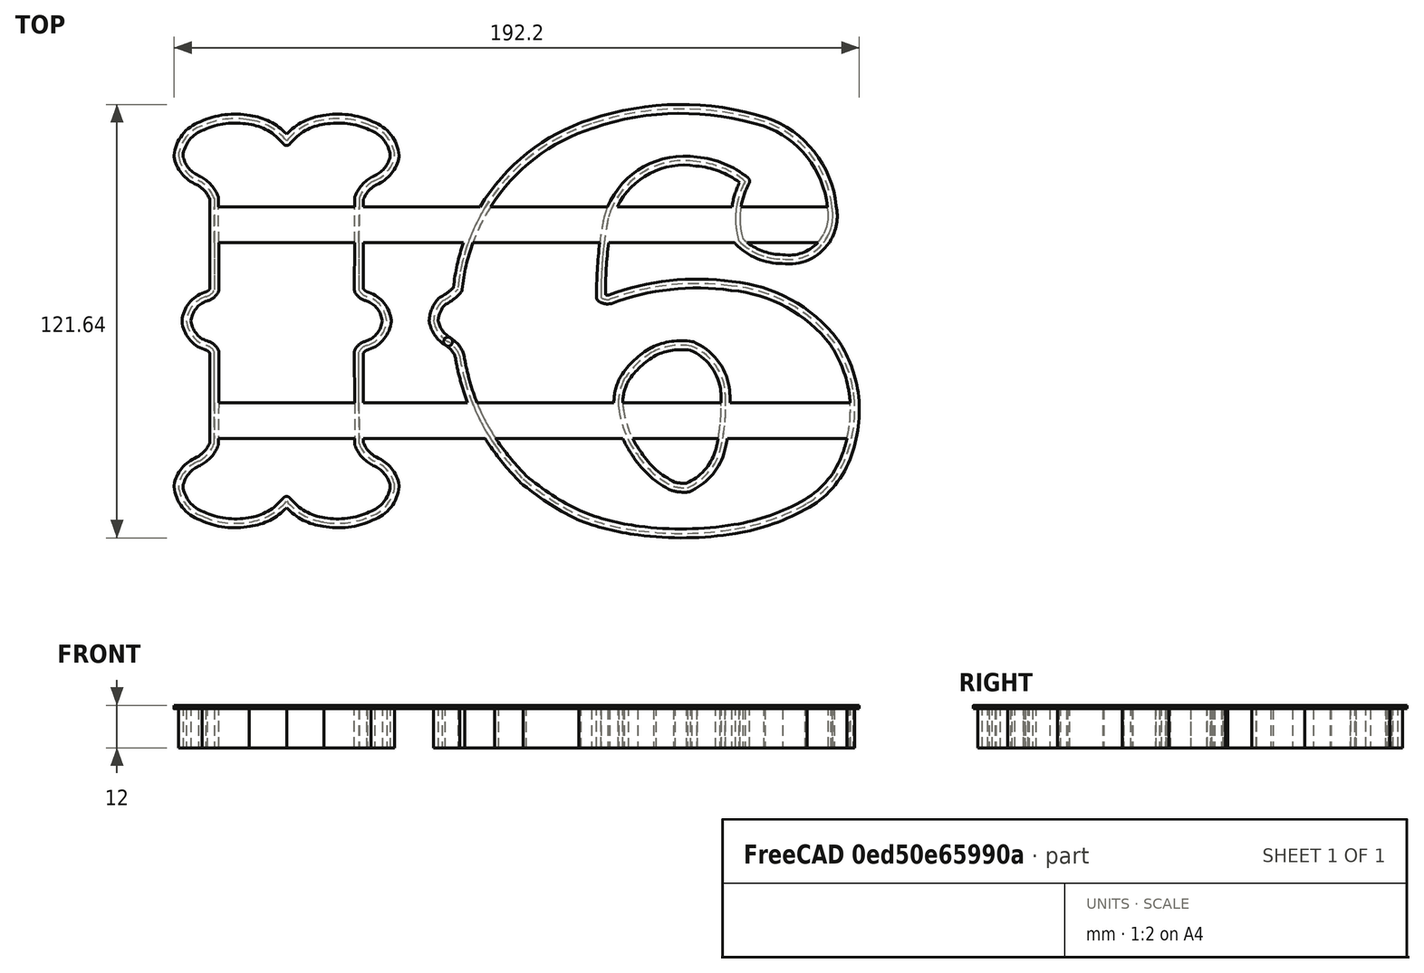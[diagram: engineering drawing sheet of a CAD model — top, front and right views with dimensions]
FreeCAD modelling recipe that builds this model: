
FCSTD DOCUMENT  (FreeCAD 0.20R27319 (Git))
Label: NumberCutter_16
License: All rights reserved
LicenseURL: http://en.wikipedia.org/wiki/All_rights_reserved
objects: Part::Offset2D×2, Part::Extrusion×2, Part::Box×2, Part::MultiFuse×2, Image::ImagePlane×1, Sketcher::SketchObject×1, PartDesign::Body×1
note: 10 computed .brp shape members not serialized (recipe doc carries the construction recipe); baked Part::Feature solids carry a one-line shape summary decoded from their .brp

FEATURE [Image::ImagePlane] ImagePlane
  XSize = 191
  YSize = 120
FEATURE [Sketcher::SketchObject] Sketch001  label="Sketch"
  FullyConstrained = false
  MapMode = 5
  Support = -> [XY_Plane]
  sketch-geometry (67):
    g0: LineSegment StartX=-44.0949 StartY=34.442 StartZ=0 EndX=-44.1561 EndY=8.72012 EndZ=0
    g1: ArcOfCircle CenterX=-44.2555 CenterY=-0.704352 CenterZ=0 NormalX=0 NormalY=0 NormalZ=1 AngleXU=0 Radius=7.94489 StartAngle=0.0887712 EndAngle=1.24847
    g2: ArcOfCircle CenterX=-41.0719 CenterY=10.1762 CenterZ=0 NormalX=0 NormalY=0 NormalZ=1 AngleXU=0 Radius=3.4106 StartAngle=3.58267 EndAngle=4.51561
    g3: ArcOfCircle CenterX=-51.9319 CenterY=40.6835 CenterZ=0 NormalX=0 NormalY=0 NormalZ=1 AngleXU=0 Radius=15.899 StartAngle=1.69919 EndAngle=2.47486
    g4: ArcOfCircle CenterX=-50.005 CenterY=34.6117 CenterZ=0 NormalX=0 NormalY=0 NormalZ=1 AngleXU=0 Radius=22.1964 StartAngle=1.13736 EndAngle=1.75028
    g5: ArcOfCircle CenterX=-43.9763 CenterY=45.3788 CenterZ=0 NormalX=0 NormalY=0 NormalZ=1 AngleXU=0 Radius=9.93843 StartAngle=0.0999134 EndAngle=1.23302
    g6: ArcOfCircle CenterX=-43.0231 CenterY=47.8373 CenterZ=0 NormalX=0 NormalY=0 NormalZ=1 AngleXU=0 Radius=9.05532 StartAngle=5.08333 EndAngle=6.12044
    g7: ArcOfCircle CenterX=-35.5185 CenterY=31.2976 CenterZ=0 NormalX=0 NormalY=0 NormalZ=1 AngleXU=0 Radius=9.13456 StartAngle=2.05128 EndAngle=2.79018
    g8: LineSegment StartX=-84.7572 StartY=34.442 StartZ=0 EndX=-84.6959 EndY=8.72012 EndZ=0
    g9: ArcOfCircle CenterX=-84.5965 CenterY=-0.704352 CenterZ=0 NormalX=0 NormalY=0 NormalZ=1 AngleXU=0 Radius=7.94489 StartAngle=1.89313 EndAngle=3.05282
    g10: ArcOfCircle CenterX=-87.7801 CenterY=10.1762 CenterZ=0 NormalX=0 NormalY=0 NormalZ=1 AngleXU=0 Radius=3.4106 StartAngle=4.90916 EndAngle=5.8421
    g11: ArcOfCircle CenterX=-76.9201 CenterY=40.6835 CenterZ=0 NormalX=0 NormalY=0 NormalZ=1 AngleXU=0 Radius=15.899 StartAngle=0.666734 EndAngle=1.4424
    g12: ArcOfCircle CenterX=-78.847 CenterY=34.6117 CenterZ=0 NormalX=0 NormalY=0 NormalZ=1 AngleXU=0 Radius=22.1964 StartAngle=1.39131 EndAngle=2.00423
    g13: ArcOfCircle CenterX=-84.8757 CenterY=45.3788 CenterZ=0 NormalX=0 NormalY=0 NormalZ=1 AngleXU=0 Radius=9.93843 StartAngle=1.90858 EndAngle=3.04168
    g14: ArcOfCircle CenterX=-85.8289 CenterY=47.8373 CenterZ=0 NormalX=0 NormalY=0 NormalZ=1 AngleXU=0 Radius=9.05532 StartAngle=3.30434 EndAngle=4.34144
    g15: ArcOfCircle CenterX=-93.3335 CenterY=31.2976 CenterZ=0 NormalX=0 NormalY=0 NormalZ=1 AngleXU=0 Radius=9.13456 StartAngle=0.35141 EndAngle=1.09032
    g16: LineSegment StartX=-44.0949 StartY=-34.442 StartZ=0 EndX=-44.1561 EndY=-8.72012 EndZ=0
    g17: ArcOfCircle CenterX=-44.2555 CenterY=0.704352 CenterZ=0 NormalX=0 NormalY=0 NormalZ=1 AngleXU=0 Radius=7.94489 StartAngle=5.03472 EndAngle=6.19441
    g18: ArcOfCircle CenterX=-41.0719 CenterY=-10.1762 CenterZ=0 NormalX=0 NormalY=0 NormalZ=1 AngleXU=0 Radius=3.4106 StartAngle=1.76757 EndAngle=2.70051
    g19: ArcOfCircle CenterX=-51.9319 CenterY=-40.6835 CenterZ=0 NormalX=0 NormalY=0 NormalZ=1 AngleXU=0 Radius=15.899 StartAngle=3.80833 EndAngle=4.58399
    g20: ArcOfCircle CenterX=-50.005 CenterY=-34.6117 CenterZ=0 NormalX=0 NormalY=0 NormalZ=1 AngleXU=0 Radius=22.1964 StartAngle=4.5329 EndAngle=5.14582
    g21: ArcOfCircle CenterX=-43.9763 CenterY=-45.3788 CenterZ=0 NormalX=0 NormalY=0 NormalZ=1 AngleXU=0 Radius=9.93843 StartAngle=5.05017 EndAngle=6.18327
    g22: ArcOfCircle CenterX=-43.0231 CenterY=-47.8373 CenterZ=0 NormalX=0 NormalY=0 NormalZ=1 AngleXU=0 Radius=9.05532 StartAngle=0.162744 EndAngle=1.19985
    g23: ArcOfCircle CenterX=-35.5185 CenterY=-31.2976 CenterZ=0 NormalX=0 NormalY=0 NormalZ=1 AngleXU=0 Radius=9.13456 StartAngle=3.493 EndAngle=4.23191
    g24: LineSegment StartX=-84.7572 StartY=-34.442 StartZ=0 EndX=-84.6959 EndY=-8.72012 EndZ=0
    g25: ArcOfCircle CenterX=-84.5965 CenterY=0.704352 CenterZ=0 NormalX=0 NormalY=0 NormalZ=1 AngleXU=0 Radius=7.94489 StartAngle=3.23036 EndAngle=4.39006
    g26: ArcOfCircle CenterX=-87.7801 CenterY=-10.1762 CenterZ=0 NormalX=0 NormalY=0 NormalZ=1 AngleXU=0 Radius=3.4106 StartAngle=0.441081 EndAngle=1.37402
    g27: ArcOfCircle CenterX=-76.9201 CenterY=-40.6835 CenterZ=0 NormalX=0 NormalY=0 NormalZ=1 AngleXU=0 Radius=15.899 StartAngle=4.84079 EndAngle=5.61645
    g28: ArcOfCircle CenterX=-78.847 CenterY=-34.6117 CenterZ=0 NormalX=0 NormalY=0 NormalZ=1 AngleXU=0 Radius=22.1964 StartAngle=4.27895 EndAngle=4.89188
    g29: ArcOfCircle CenterX=-84.8757 CenterY=-45.3788 CenterZ=0 NormalX=0 NormalY=0 NormalZ=1 AngleXU=0 Radius=9.93843 StartAngle=3.24151 EndAngle=4.37461
    g30: ArcOfCircle CenterX=-85.8289 CenterY=-47.8373 CenterZ=0 NormalX=0 NormalY=0 NormalZ=1 AngleXU=0 Radius=9.05532 StartAngle=1.94174 EndAngle=2.97885
    g31: ArcOfCircle CenterX=-93.3335 CenterY=-31.2976 CenterZ=0 NormalX=0 NormalY=0 NormalZ=1 AngleXU=0 Radius=9.13456 StartAngle=5.19287 EndAngle=5.93178
    g32: ArcOfCircle CenterX=-14.3118 CenterY=-0.477089 CenterZ=0 NormalX=0 NormalY=0 NormalZ=1 AngleXU=0 Radius=8.88675 StartAngle=2.40162 EndAngle=3.08788
    g33: ArcOfCircle CenterX=-26.693 CenterY=17.7972 CenterZ=0 NormalX=0 NormalY=0 NormalZ=1 AngleXU=0 Radius=13.5907 StartAngle=5.1548 EndAngle=5.56991
    g34: ArcOfCircle CenterX=37.4429 CenterY=3.76243 CenterZ=0 NormalX=0 NormalY=0 NormalZ=1 AngleXU=0 Radius=54.1032 StartAngle=1.87661 EndAngle=3.0464
    g35: ArcOfCircle CenterX=46.2531 CenterY=-18.3508 CenterZ=0 NormalX=0 NormalY=0 NormalZ=1 AngleXU=0 Radius=77.8624 StartAngle=1.26469 EndAngle=1.89901
    g36: ArcOfCircle CenterX=60.5001 CenterY=29.3101 CenterZ=0 NormalX=0 NormalY=0 NormalZ=1 AngleXU=0 Radius=28.1345 StartAngle=0.0982451 EndAngle=1.23706
    g37: ArcOfCircle CenterX=76.4612 CenterY=29.5329 CenterZ=0 NormalX=0 NormalY=0 NormalZ=1 AngleXU=0 Radius=12.3022 StartAngle=4.56544 EndAngle=6.49089
    g38: ArcOfCircle CenterX=74.616 CenterY=34.4646 CenterZ=0 NormalX=0 NormalY=0 NormalZ=1 AngleXU=0 Radius=17.1014 StartAngle=3.91734 EndAngle=4.71496
    g39: ArcOfCircle CenterX=82.9352 CenterY=28.7211 CenterZ=0 NormalX=0 NormalY=0 NormalZ=1 AngleXU=0 Radius=21.4529 StartAngle=2.63178 EndAngle=3.43632
    g40: ArcOfCircle CenterX=48.4504 CenterY=19.9812 CenterZ=0 NormalX=0 NormalY=0 NormalZ=1 AngleXU=0 Radius=24.8469 StartAngle=0.883715 EndAngle=1.48558
    g41: ArcOfCircle CenterX=47.0715 CenterY=22.9255 CenterZ=0 NormalX=0 NormalY=0 NormalZ=1 AngleXU=0 Radius=22.0904 StartAngle=1.41197 EndAngle=2.88283
    g42: ArcOfCircle CenterX=133.219 CenterY=7.96319 CenterZ=0 NormalX=0 NormalY=0 NormalZ=1 AngleXU=0 Radius=109.461 StartAngle=2.95213 EndAngle=3.1543
    g43: ArcOfCircle CenterX=25.6086 CenterY=9.36331 CenterZ=0 NormalX=0 NormalY=0 NormalZ=1 AngleXU=0 Radius=3.34395 StartAngle=4.12901 EndAngle=4.88585
    g44: ArcOfCircle CenterX=50.6675 CenterY=-59.4009 CenterZ=0 NormalX=0 NormalY=0 NormalZ=1 AngleXU=0 Radius=69.8981 StartAngle=1.43149 EndAngle=1.92863
    g45: ArcOfCircle CenterX=56.849 CenterY=-30.6384 CenterZ=0 NormalX=0 NormalY=0 NormalZ=1 AngleXU=0 Radius=40.6116 StartAngle=0.652321 EndAngle=1.48392
    g46: ArcOfCircle CenterX=59.698 CenterY=-25.5465 CenterZ=0 NormalX=0 NormalY=0 NormalZ=1 AngleXU=0 Radius=35.3327 StartAngle=0.183618 EndAngle=0.586697
    g47: ArcOfCircle CenterX=59.1415 CenterY=-25.0675 CenterZ=0 NormalX=0 NormalY=0 NormalZ=1 AngleXU=0 Radius=35.797 StartAngle=5.93472 EndAngle=6.45081
    g48: ArcOfCircle CenterX=68.5744 CenterY=-29.2445 CenterZ=0 NormalX=0 NormalY=0 NormalZ=1 AngleXU=0 Radius=25.5145 StartAngle=5.24515 EndAngle=5.96235
    g49: ArcOfCircle CenterX=51.6917 CenterY=0.785216 CenterZ=0 NormalX=0 NormalY=0 NormalZ=1 AngleXU=0 Radius=59.9615 StartAngle=4.87202 EndAngle=5.23332
    g50: ArcOfCircle CenterX=46.2762 CenterY=32.5071 CenterZ=0 NormalX=0 NormalY=0 NormalZ=1 AngleXU=0 Radius=92.1414 StartAngle=4.58208 EndAngle=4.87532
    g51: ArcOfCircle CenterX=42.2772 CenterY=6.73465 CenterZ=0 NormalX=0 NormalY=0 NormalZ=1 AngleXU=0 Radius=66.0707 StartAngle=4.32807 EndAngle=4.5914
    g52: ArcOfCircle CenterX=49.2357 CenterY=11.0915 CenterZ=0 NormalX=0 NormalY=0 NormalZ=1 AngleXU=0 Radius=72.8781 StartAngle=4.00513 EndAngle=4.26192
    g53: ArcOfCircle CenterX=58.6775 CenterY=11.2759 CenterZ=0 NormalX=0 NormalY=0 NormalZ=1 AngleXU=0 Radius=79.4671 StartAngle=3.75871 EndAngle=3.9162
    g54: ArcOfCircle CenterX=40.8052 CenterY=-2.28447 CenterZ=0 NormalX=0 NormalY=0 NormalZ=1 AngleXU=0 Radius=57.0486 StartAngle=3.39119 EndAngle=3.74615
    g55: ArcOfCircle CenterX=38.9149 CenterY=-1.25283 CenterZ=0 NormalX=0 NormalY=0 NormalZ=1 AngleXU=0 Radius=55.4911 StartAngle=3.29753 EndAngle=3.41762
    g56: ArcOfCircle CenterX=-22.8727 CenterY=-12.1054 CenterZ=0 NormalX=0 NormalY=0 NormalZ=1 AngleXU=0 Radius=7.31918 StartAngle=0.310212 EndAngle=1.03585
    g57: ArcOfCircle CenterX=-14.7928 CenterY=1.53128 CenterZ=0 NormalX=0 NormalY=0 NormalZ=1 AngleXU=0 Radius=8.5315 StartAngle=3.32206 EndAngle=4.17754
    g58: ArcOfCircle CenterX=43.1477 CenterY=-21.4122 CenterZ=0 NormalX=0 NormalY=0 NormalZ=1 AngleXU=0 Radius=15.5785 StartAngle=0.172564 EndAngle=1.17541
    g59: ArcOfCircle CenterX=7.15552 CenterY=-23.7166 CenterZ=0 NormalX=0 NormalY=0 NormalZ=1 AngleXU=0 Radius=51.5801 StartAngle=6.02427 EndAngle=6.37987
    g60: ArcOfCircle CenterX=41.7256 CenterY=-31.9954 CenterZ=0 NormalX=0 NormalY=0 NormalZ=1 AngleXU=0 Radius=16.0651 StartAngle=5.1123 EndAngle=5.97144
    g61: ArcOfCircle CenterX=47.0754 CenterY=-35.0507 CenterZ=0 NormalX=0 NormalY=0 NormalZ=1 AngleXU=0 Radius=11.777 StartAngle=4.45535 EndAngle=4.78931
    g62: ArcOfCircle CenterX=54.4423 CenterY=-24.4593 CenterZ=0 NormalX=0 NormalY=0 NormalZ=1 AngleXU=0 Radius=24.3009 StartAngle=3.71228 EndAngle=4.27192
    g63: ArcOfCircle CenterX=57.1795 CenterY=-20.5968 CenterZ=0 NormalX=0 NormalY=0 NormalZ=1 AngleXU=0 Radius=28.7456 StartAngle=3.27924 EndAngle=3.77395
    g64: ArcOfCircle CenterX=42.8143 CenterY=-22.967 CenterZ=0 NormalX=0 NormalY=0 NormalZ=1 AngleXU=0 Radius=14.196 StartAngle=2.64973 EndAngle=3.2527
    g65: ArcOfCircle CenterX=50.3544 CenterY=-29.4284 CenterZ=0 NormalX=0 NormalY=0 NormalZ=1 AngleXU=0 Radius=23.9889 StartAngle=2.08701 EndAngle=2.56064
    g66: ArcOfCircle CenterX=46.2508 CenterY=-24.6241 CenterZ=0 NormalX=0 NormalY=0 NormalZ=1 AngleXU=0 Radius=17.8255 StartAngle=1.40755 EndAngle=2.01978
  constraints (69):
    c: PointOnObject(g1,g-1)
    c: Coincident(g2,g1)
    c: Coincident(g4,g3)
    c: Coincident(g5,g4)
    c: Coincident(g6,g5)
    c: Coincident(g7,g6)
    c: Coincident(g7,g0)
    c: Coincident(g10,g9)
    c: Coincident(g12,g11)
    c: Coincident(g13,g12)
    c: Coincident(g14,g13)
    c: Coincident(g15,g14)
    c: Coincident(g15,g8)
    c: Coincident(g18,g17)
    c: Coincident(g20,g19)
    c: Coincident(g21,g20)
    c: Coincident(g22,g21)
    c: Coincident(g23,g22)
    c: Coincident(g23,g16)
    c: Coincident(g26,g25)
    c: Coincident(g28,g27)
    c: Coincident(g29,g28)
    c: Coincident(g30,g29)
    c: Coincident(g31,g30)
    c: Coincident(g31,g24)
    c: PointOnObject(g32,g-1)
    c: Coincident(g33,g32)
    c: Coincident(g34,g33)
    c: Coincident(g35,g34)
    c: Coincident(g36,g35)
    c: Coincident(g37,g36)
    c: Coincident(g38,g37)
    c: Coincident(g40,g39)
    c: Coincident(g41,g40)
    c: Coincident(g42,g41)
    c: Coincident(g44,g43)
    c: Coincident(g45,g44)
    c: Coincident(g46,g45)
    c: Coincident(g47,g46)
    c: Coincident(g48,g47)
    c: Coincident(g49,g48)
    c: Coincident(g50,g49)
    c: Coincident(g51,g50)
    c: Coincident(g52,g51)
    c: Coincident(g53,g52)
    c: Coincident(g54,g53)
    c: Coincident(g55,g54)
    c: Coincident(g56,g55)
    c: Coincident(g57,g32)
    c: Coincident(g57,g56)
    c: Coincident(g59,g58)
    c: Coincident(g60,g59)
    c: Coincident(g61,g60)
    c: Coincident(g62,g61)
    c: Coincident(g63,g62)
    c: Coincident(g64,g63)
    c: Coincident(g65,g64)
    c: Coincident(g66,g65)
    c: Coincident(g66,g58)
    c: Coincident(g42,g43)
    c: Coincident(g3,g11)
    c: Coincident(g8,g10)
    c: Coincident(g9,g25)
    c: Coincident(g24,g26)
    c: Coincident(g19,g27)
    c: Coincident(g1,g17)
    c: Coincident(g16,g18)
    c: Coincident(g0,g2)
    c: Coincident(g38,g39)
FEATURE [PartDesign::Body] Body  label="Number Outline"
  Group = -> [Sketch001]
  Origin = -> Origin
FEATURE [Part::Offset2D] Offset2D
  Fill = true
  Intersection = false
  Join = 0
  Mode = 1
  SelfIntersection = false
  Source = -> Sketch001
  Value = -1.25
FEATURE [Part::Extrusion] Extrude  label="Cutter Walls"
  Base = -> Offset2D
  Dir = (0,0,1)
  DirMode = 2
  FaceMakerClass = Part::FaceMakerBullseye
  LengthFwd = 12
  LengthRev = 0
  Reversed = true
  Solid = false
  Symmetric = false
FEATURE [Part::Box] Box  label="Support 1"
  AttacherType = Attacher::AttachEngine3D
  Height = 1
  Length = 173
  Placement = pos=(-85,22,-1) rot=(0,0,1;0rad)
  Width = 10
FEATURE [Part::Box] Box001  label="Support 2"
  AttacherType = Attacher::AttachEngine3D
  Height = 1
  Length = 180
  Placement = pos=(-85,-33,-1) rot=(0,0,1;0rad)
  Width = 10
FEATURE [Part::MultiFuse] Fusion  label="Thin Wall"
  Shapes = -> [Extrude,Box,Box001]
FEATURE [Part::Offset2D] Offset2D001
  Fill = true
  Intersection = false
  Join = 0
  Mode = 1
  SelfIntersection = false
  Source = -> Sketch001
  Value = 1.25
FEATURE [Part::Extrusion] Extrude001  label="Reinforcing"
  Base = -> Offset2D001
  Dir = (0,0,1)
  DirMode = 2
  FaceMakerClass = Part::FaceMakerBullseye
  LengthFwd = 1
  LengthRev = 0
  Reversed = true
  Solid = false
  Symmetric = false
FEATURE [Part::MultiFuse] Fusion001  label="Cutter"
  Shapes = -> [Extrude001,Fusion]
